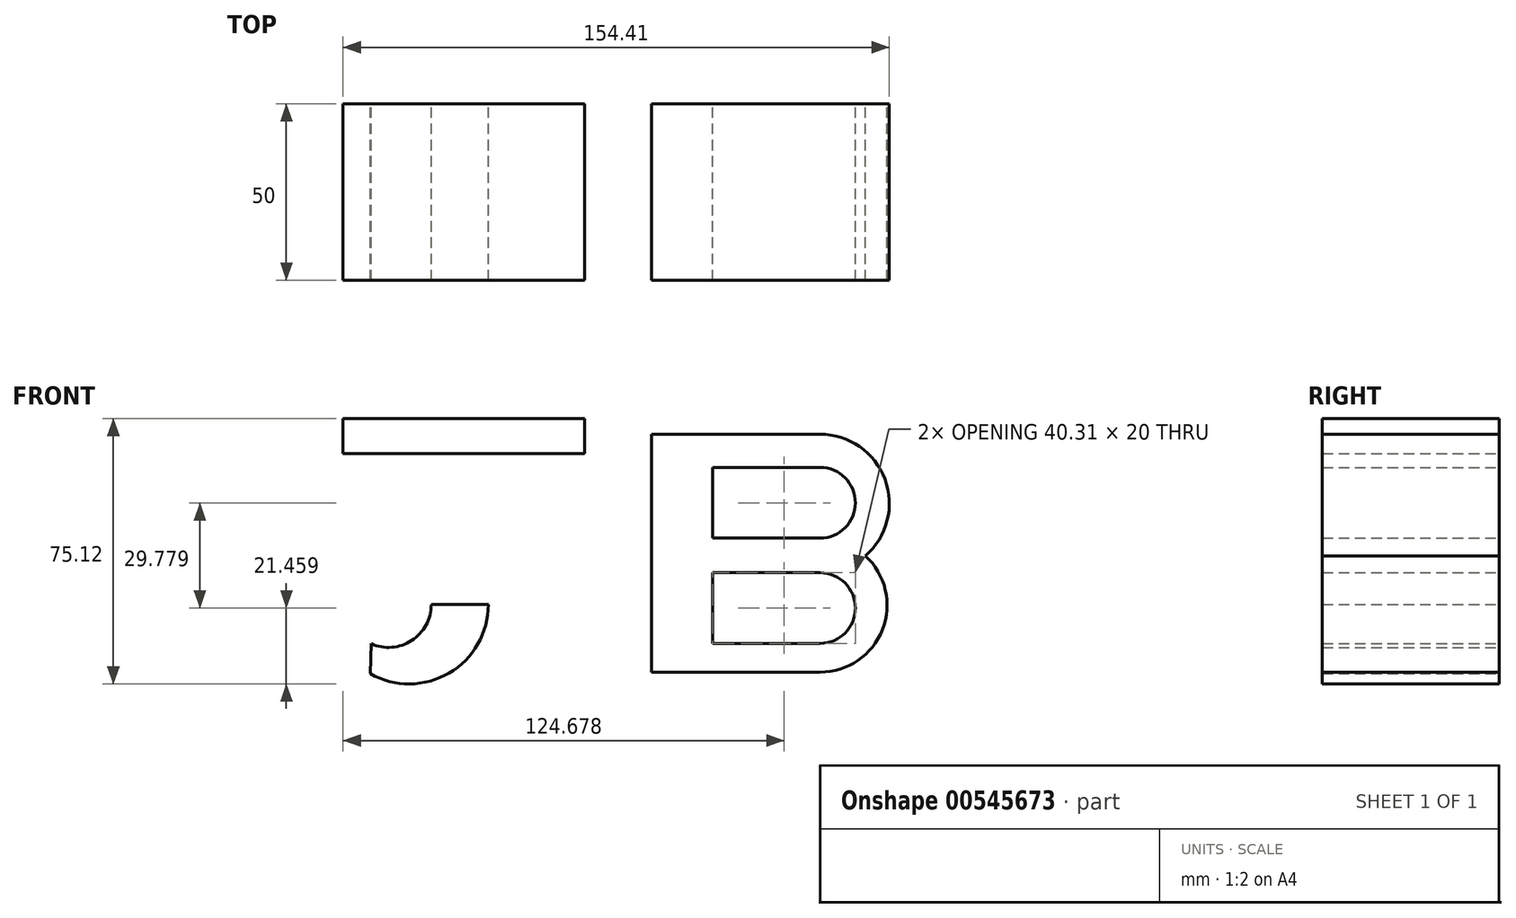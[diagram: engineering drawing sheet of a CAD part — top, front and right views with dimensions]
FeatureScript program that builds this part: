
annotation { "Feature Type Name" : "Feature", "Feature Type Description" : "" }
export const myFeature = defineFeature(function(context is Context, id is Id, definition is map)
    precondition{}
    {
        {
            var Q0;
            Q0=qCreatedBy(makeId("Front.planeOp"),FACE);
            var sketch = newSketch(context, id + "F0", { "sketchPlane" : qUnion([Q0])});
            skLineSegment(sketch, "E0.bottom", {"start": v(-72.23, 52.69) * mm, "end": v(-3.97, 52.69) * mm});
            skLineSegment(sketch, "E0.top", {"start": v(-72.23, 42.77) * mm, "end": v(-3.97, 42.77) * mm});
            skLineSegment(sketch, "E0.left", {"start": v(-72.23, 52.69) * mm, "end": v(-72.23, 42.77) * mm});
            skLineSegment(sketch, "E0.right", {"start": v(-3.97, 52.69) * mm, "end": v(-3.97, 42.77) * mm});
            skLineSegment(sketch, "E1.bottom", {"start": v(-47.3, 42.77) * mm, "end": v(-31.16, 42.77) * mm});
            skLineSegment(sketch, "E1.top", {"start": v(-47.3, 0) * mm, "end": v(-31.16, 0) * mm});
            skLineSegment(sketch, "E1.left", {"start": v(-47.3, 42.77) * mm, "end": v(-47.3, 0) * mm});
            skLineSegment(sketch, "E1.right", {"start": v(-31.16, 42.77) * mm, "end": v(-31.16, 0) * mm});
            skArc(sketch, "E2", {"start": v(-64.3, -11.05) * mm, "mid": v(-52.8, -10.14) * mm, "end": v(-47.3, 0) * mm});
            skArc(sketch, "E3", {"start": v(-64.59, -19.55) * mm, "mid": v(-42.27, -19.36) * mm, "end": v(-31.16, 0) * mm});
            skLineSegment(sketch, "E4", {"start": v(-64.3, -11.05) * mm, "end": v(-64.59, -19.55) * mm});
            skSolve(sketch);
        }
        {
            var Q0;
            Q0=qCreatedBy(makeId("Front.planeOp"),FACE);
            var sketch = newSketch(context, id + "F1", { "sketchPlane" : qUnion([Q0])});
            skLineSegment(sketch, "E5.bottom", {"start": v(15.01, 48.2) * mm, "end": v(32.3, 48.2) * mm});
            skLineSegment(sketch, "E5.top", {"start": v(15.01, -19.1) * mm, "end": v(32.3, -19.1) * mm});
            skLineSegment(sketch, "E5.left", {"start": v(15.01, 48.2) * mm, "end": v(15.01, -19.1) * mm});
            skLineSegment(sketch, "E5.right", {"start": v(32.3, 48.2) * mm, "end": v(32.3, -19.1) * mm});
            skLineSegment(sketch, "E6.bottom", {"start": v(32.3, 48.2) * mm, "end": v(62.6, 48.2) * mm});
            skLineSegment(sketch, "E6.top", {"start": v(32.3, 38.8) * mm, "end": v(62.6, 38.8) * mm});
            skLineSegment(sketch, "E6.left", {"start": v(32.3, 48.2) * mm, "end": v(32.3, 38.8) * mm});
            skLineSegment(sketch, "E6.right", {"start": v(62.6, 48.2) * mm, "end": v(62.6, 38.8) * mm});
            skLineSegment(sketch, "E7.bottom", {"start": v(32.3, 18.8) * mm, "end": v(62.6, 18.8) * mm});
            skLineSegment(sketch, "E7.top", {"start": v(32.3, 9.03) * mm, "end": v(62.6, 9.03) * mm});
            skLineSegment(sketch, "E7.left", {"start": v(32.3, 18.8) * mm, "end": v(32.3, 9.03) * mm});
            skLineSegment(sketch, "E7.right", {"start": v(62.6, 18.8) * mm, "end": v(62.6, 9.03) * mm});
            skLineSegment(sketch, "E8.bottom", {"start": v(32.3, -19.1) * mm, "end": v(62.6, -19.1) * mm});
            skLineSegment(sketch, "E8.top", {"start": v(32.3, -10.97) * mm, "end": v(62.6, -10.97) * mm});
            skLineSegment(sketch, "E8.left", {"start": v(32.3, -19.1) * mm, "end": v(32.3, -10.97) * mm});
            skLineSegment(sketch, "E8.right", {"start": v(62.6, -19.1) * mm, "end": v(62.6, -10.97) * mm});
            skArc(sketch, "E9", {"start": v(62.6, -10.97) * mm, "mid": v(72.6, -0.97) * mm, "end": v(62.6, 9.03) * mm});
            skArc(sketch, "E10", {"start": v(62.6, -19.1) * mm, "mid": v(81.55, -0.14) * mm, "end": v(62.6, 18.8) * mm});
            skArc(sketch, "E11", {"start": v(62.6, 9.03) * mm, "mid": v(82.18, 28.61) * mm, "end": v(62.6, 48.2) * mm});
            skArc(sketch, "E12", {"start": v(62.6, 18.8) * mm, "mid": v(72.6, 28.8) * mm, "end": v(62.6, 38.8) * mm});
            skSolve(sketch);
        }
        {
            var Q0;
            Q0=makeQuery(id+"F1.imprint","IMPRINT",FACE,{"disambiguationData":[TD([[makeQuery(id+"F1.imprint","IMPRINT",EDGE,{"derivedFrom":sQuery(id+"F1.wireOp",EDGE,"E5.bottom")}),-1.0]])]});
            var Q1;
            Q1=makeQuery(id+"F1.imprint","IMPRINT",FACE,{"disambiguationData":[TD([[makeQuery(id+"F1.imprint","IMPRINT",EDGE,{"derivedFrom":sQuery(id+"F1.wireOp",EDGE,"E6.bottom")}),-1.0]])]});
            var Q2;
            Q2=makeQuery(id+"F1.imprint","IMPRINT",FACE,{"disambiguationData":[TD([[makeQuery(id+"F1.imprint","IMPRINT",EDGE,{"derivedFrom":sQuery(id+"F1.wireOp",EDGE,"E8.bottom")}),1.0]])]});
            var Q3;
            Q3=makeQuery(id+"F1.imprint","IMPRINT",FACE,{"disambiguationData":[TD([[makeQuery(id+"F1.imprint","IMPRINT",EDGE,{"derivedFrom":sQuery(id+"F1.wireOp",EDGE,"E7.bottom")}),-1.0]])]});
            var Q4;
            {var subQ0=sQuery(id+"F1.wireOp",EDGE,"E7.right");Q4=makeQuery(id+"F1.imprint","IMPRINT",FACE,{"disambiguationData":[TD([[makeQuery(id+"F1.imprint","IMPRINT",EDGE,{"derivedFrom":subQ0}),1.0]])]});}
            var Q5;
            {var subQ0=sQuery(id+"F1.wireOp",EDGE,"E8.right");Q5=makeQuery(id+"F1.imprint","IMPRINT",FACE,{"disambiguationData":[TD([[makeQuery(id+"F1.imprint","IMPRINT",EDGE,{"derivedFrom":subQ0}),-1.0]])]});}
            var Q6;
            {var subQ0=sQuery(id+"F1.wireOp",EDGE,"E6.right");Q6=makeQuery(id+"F1.imprint","IMPRINT",FACE,{"disambiguationData":[TD([[makeQuery(id+"F1.imprint","IMPRINT",EDGE,{"derivedFrom":subQ0}),1.0]])]});}
            var Q7;
            Q7=makeQuery(id+"F0.imprint","IMPRINT",FACE,{"disambiguationData":[TD([[makeQuery(id+"F0.imprint","IMPRINT",EDGE,{"derivedFrom":sQuery(id+"F0.wireOp",EDGE,"E1.bottom")}),-1.0]])]});
            var Q8;
            Q8=makeQuery(id+"F0.imprint","IMPRINT",FACE,{"disambiguationData":[TD([[makeQuery(id+"F0.imprint","IMPRINT",EDGE,{"derivedFrom":sQuery(id+"F0.wireOp",EDGE,"E1.top")}),-1.0]])]});
            var Q9;
            Q9=makeQuery(id+"F0.imprint","IMPRINT",FACE,{"disambiguationData":[TD([[makeQuery(id+"F0.imprint","IMPRINT",EDGE,{"derivedFrom":sQuery(id+"F0.wireOp",EDGE,"E0.bottom")}),-1.0]])]});
            extrude(context, id + "F2", {"entities" : qUnion([Q0, Q1, Q2, Q3, Q4, Q5, Q6, Q7, Q8, Q9]), "depth" : 50 * mm, "offsetDistance" : 25 * mm});
        }
    });
